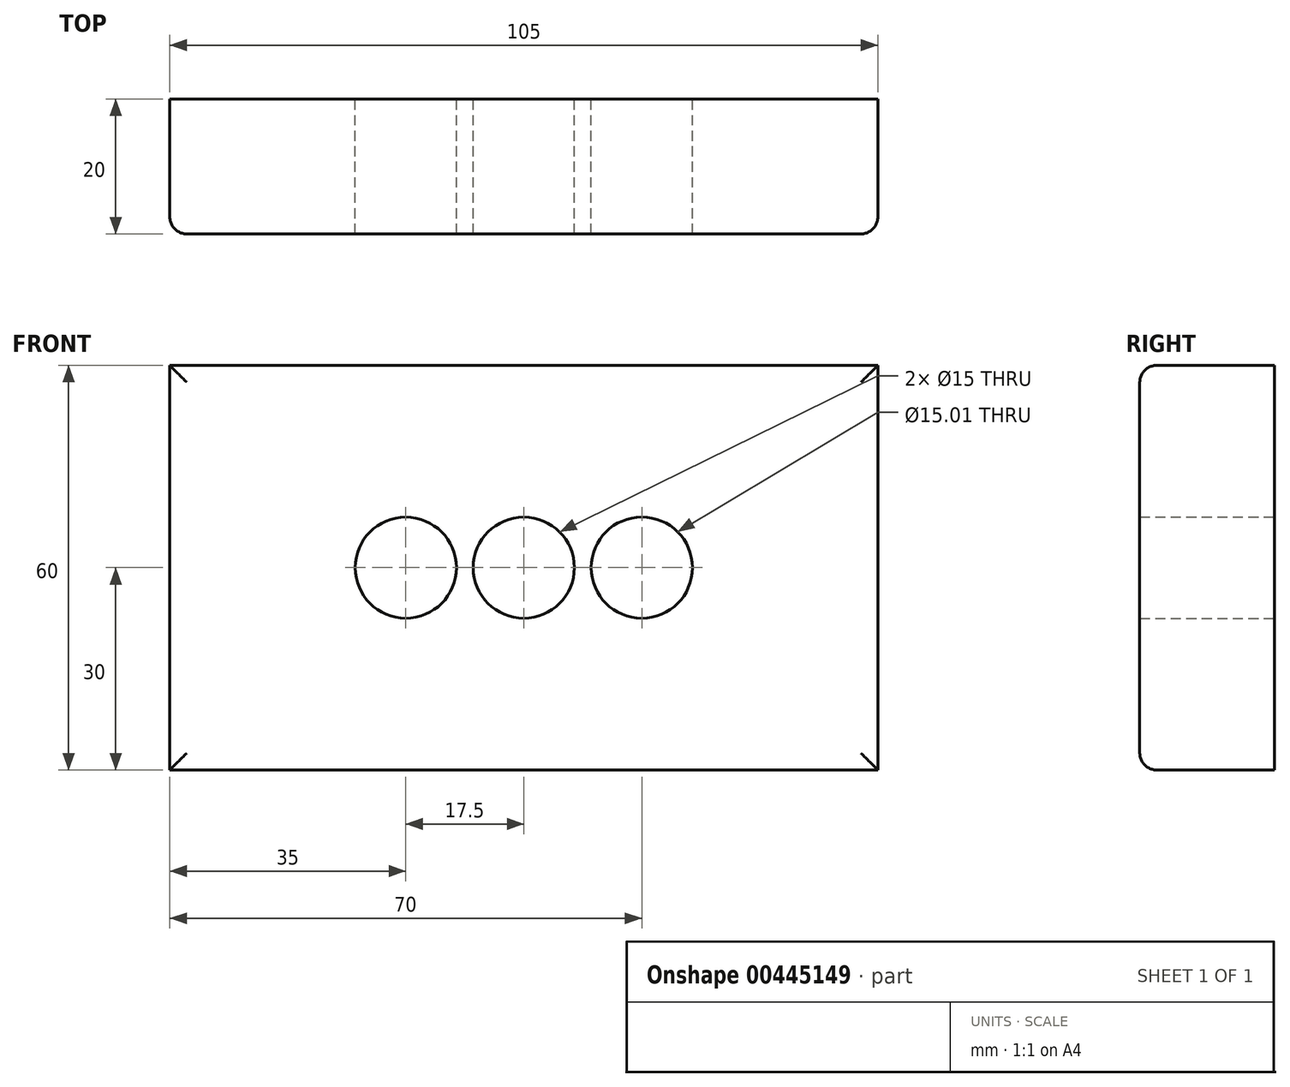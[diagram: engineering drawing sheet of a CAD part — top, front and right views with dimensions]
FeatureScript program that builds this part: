
annotation { "Feature Type Name" : "Feature", "Feature Type Description" : "" }
export const myFeature = defineFeature(function(context is Context, id is Id, definition is map)
    precondition{}
    {
        {
            var Q0;
            Q0=qCreatedBy(makeId("Front.planeOp"),FACE);
            var sketch = newSketch(context, id + "F0", { "sketchPlane" : qUnion([Q0])});
            skLineSegment(sketch, "E0.bottom", {"start": v(-52.5, 30) * mm, "end": v(52.5, 30) * mm});
            skLineSegment(sketch, "E0.top", {"start": v(-52.5, -30) * mm, "end": v(52.5, -30) * mm});
            skLineSegment(sketch, "E0.left", {"start": v(-52.5, 30) * mm, "end": v(-52.5, -30) * mm});
            skLineSegment(sketch, "E0.right", {"start": v(52.5, 30) * mm, "end": v(52.5, -30) * mm});
            skPoint(sketch, "E0.middle", {"position": v(0, 0) * mm});
            skCircle(sketch, "E1", {"center": v(0, 0) * mm, "radius": 7.5 * mm});
            skCircle(sketch, "E2", {"center": v(-17.5, 0) * mm, "radius": 7.5 * mm});
            skCircle(sketch, "E3", {"center": v(17.5, 0) * mm, "radius": 7.5 * mm});
            skSolve(sketch);
        }
        {
            var Q0;
            Q0=makeQuery(id+"F0.imprint","IMPRINT",FACE,{"disambiguationData":[TD([[makeQuery(id+"F0.imprint","IMPRINT",EDGE,{"derivedFrom":sQuery(id+"F0.wireOp",EDGE,"E0.bottom")}),-1.0]])]});
            extrude(context, id + "F1", {"entities" : qUnion([Q0]), "depth" : 20 * mm});
        }
        {
            var Q0;
            Q0=makeQuery(id+"F1.opExtrude","CAP_EDGE",EDGE,{"disambiguationData":[OSD([sQuery(id+"F0.wireOp",EDGE,"E0.left")])],"isStart":false});
            var Q1;
            Q1=makeQuery(id+"F1.opExtrude","CAP_EDGE",EDGE,{"disambiguationData":[OSD([sQuery(id+"F0.wireOp",EDGE,"E0.bottom")])],"isStart":false});
            var Q2;
            Q2=makeQuery(id+"F1.opExtrude","CAP_EDGE",EDGE,{"disambiguationData":[OSD([sQuery(id+"F0.wireOp",EDGE,"E0.top")])],"isStart":false});
            var Q3;
            Q3=makeQuery(id+"F1.opExtrude","CAP_EDGE",EDGE,{"disambiguationData":[OSD([sQuery(id+"F0.wireOp",EDGE,"E0.right")])],"isStart":false});
            fillet(context, id + "F2", {"entities" : qUnion([Q0, Q1, Q2, Q3]), "radius" : 2.5 * mm, "tangentPropagation" : true, "allowEdgeOverflow" : false});
        }
    });
